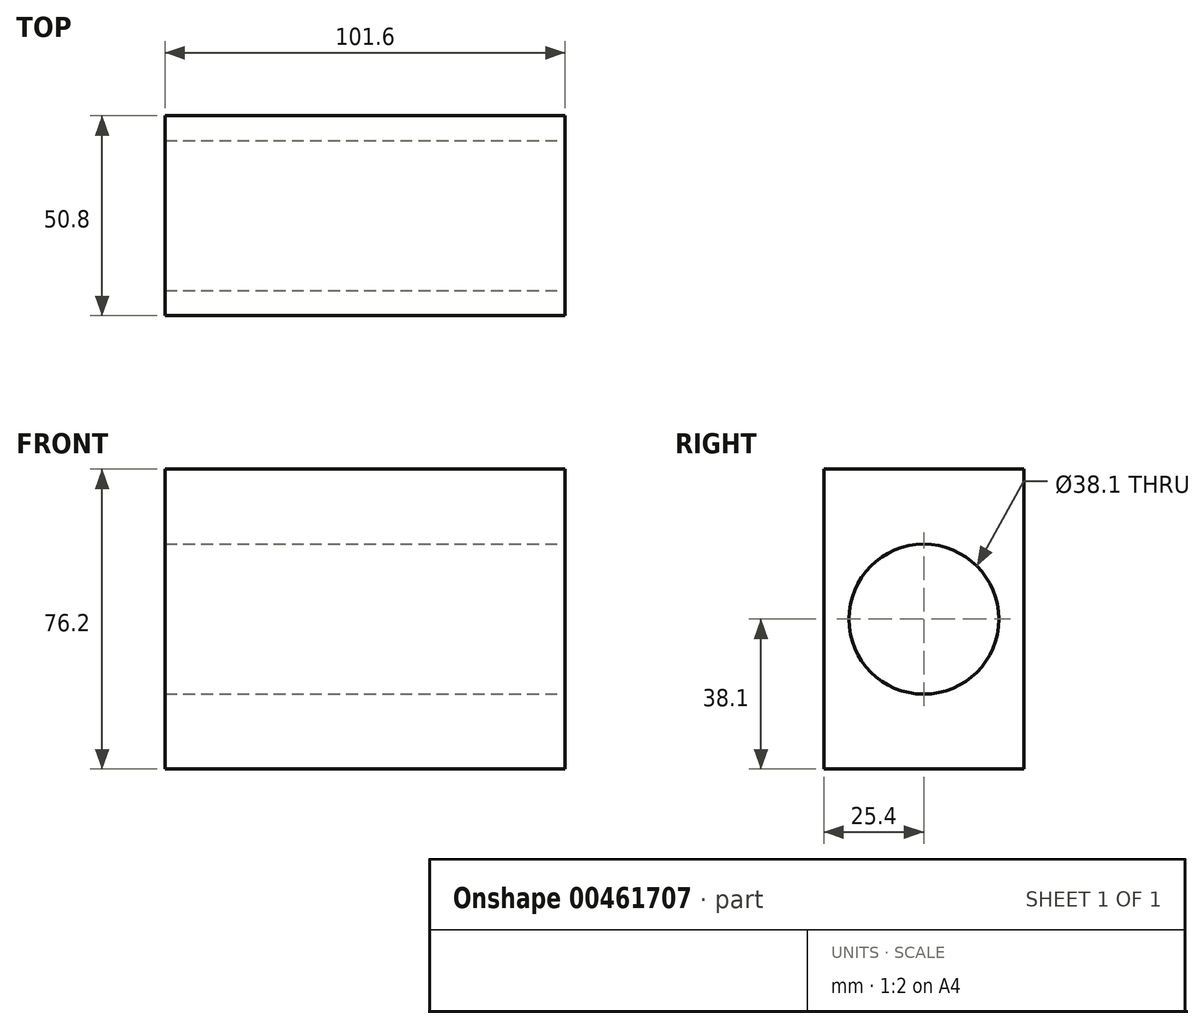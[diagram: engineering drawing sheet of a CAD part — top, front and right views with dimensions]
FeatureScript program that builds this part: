
annotation { "Feature Type Name" : "Feature", "Feature Type Description" : "" }
export const myFeature = defineFeature(function(context is Context, id is Id, definition is map)
    precondition{}
    {
        {
            var Q0;
            Q0=qCreatedBy(makeId("Top.planeOp"),FACE);
            var sketch = newSketch(context, id + "F0", { "sketchPlane" : qUnion([Q0])});
            skLineSegment(sketch, "E0.bottom", {"start": v(50.8, -25.4) * mm, "end": v(-50.8, -25.4) * mm});
            skLineSegment(sketch, "E0.top", {"start": v(50.8, 25.4) * mm, "end": v(-50.8, 25.4) * mm});
            skLineSegment(sketch, "E0.left", {"start": v(50.8, -25.4) * mm, "end": v(50.8, 25.4) * mm});
            skLineSegment(sketch, "E0.right", {"start": v(-50.8, -25.4) * mm, "end": v(-50.8, 25.4) * mm});
            skPoint(sketch, "E0.middle", {"position": v(0, 0) * mm});
            skLineSegment(sketch, "E1.bottom", {"start": v(-25.4, 25.4) * mm, "end": v(25.4, 25.4) * mm});
            skLineSegment(sketch, "E2.top", {"start": v(-25.4, 76.2) * mm, "end": v(25.4, 76.2) * mm});
            skLineSegment(sketch, "E2.left", {"start": v(-25.4, 25.4) * mm, "end": v(-25.4, 76.2) * mm});
            skLineSegment(sketch, "E2.right", {"start": v(25.4, 25.4) * mm, "end": v(25.4, 76.2) * mm});
            skSolve(sketch);
        }
        {
            var Q0;
            Q0=makeQuery(id+"F0.imprint","IMPRINT",FACE,{"disambiguationData":[TD([[makeQuery(id+"F0.imprint","IMPRINT",EDGE,{"derivedFrom":sQuery(id+"F0.wireOp",EDGE,"E0.bottom")}),-1.0]])]});
            var Q1;
            Q1=makeQuery(id+"F0.imprint","IMPRINT",FACE,{"disambiguationData":[TD([[makeQuery(id+"F0.imprint","IMPRINT",EDGE,{"derivedFrom":sQuery(id+"F0.wireOp",EDGE,"E1.bottom")}),1.0]])]});
            var Q2;
            Q2=makeQuery(id+"F0.imprint","IMPRINT",FACE,{"disambiguationData":[TD([[makeQuery(id+"F0.imprint","IMPRINT",EDGE,{"derivedFrom":sQuery(id+"F0.wireOp",EDGE,"E1.bottom")}),1.0]])]});
            extrude(context, id + "F1", {"entities" : qUnion([Q0, Q1, Q2]), "depth" : 76.2 * mm});
        }
        {
            var Q0;
            Q0=makeQuery(id+"F1.opExtrude","SWEPT_FACE",FACE,{"disambiguationData":[OSD([sQuery(id+"F0.wireOp",EDGE,"E0.left")])]});
            var sketch = newSketch(context, id + "F2", { "sketchPlane" : qUnion([Q0])});
            skCircle(sketch, "E3", {"center": v(0, 38.1) * mm, "radius": 19.05 * mm});
            skSolve(sketch);
        }
        {
            var Q0;
            Q0=sQuery(id+"F2.wireOp",VERTEX,"E3.center");
            var Q1;
            Q1=makeQuery(id+"F1.opExtrude","SWEPT_BODY",BODY,{"disambiguationData":[OSD([sQuery(id+"F0.wireOp",EDGE,"E0.bottom"),sQuery(id+"F0.wireOp",EDGE,"E0.top"),sQuery(id+"F0.wireOp",EDGE,"E0.left"),sQuery(id+"F0.wireOp",EDGE,"E0.right"),sQuery(id+"F0.wireOp",EDGE,"E2.top"),sQuery(id+"F0.wireOp",EDGE,"E2.left"),sQuery(id+"F0.wireOp",EDGE,"E2.right")])]});
            hole(context, id + "F3", {"style" : HoleStyle.SIMPLE, "endStyle" : HoleEndStyle.THROUGH, "holeDiameter" : 38.1 * mm, "isTappedThrough" : true, "tappedDepth" : 12.7 * mm, "tapClearance" : 3, "locations" : qUnion([Q0]), "scope" : qUnion([Q1])});
        }
    });
